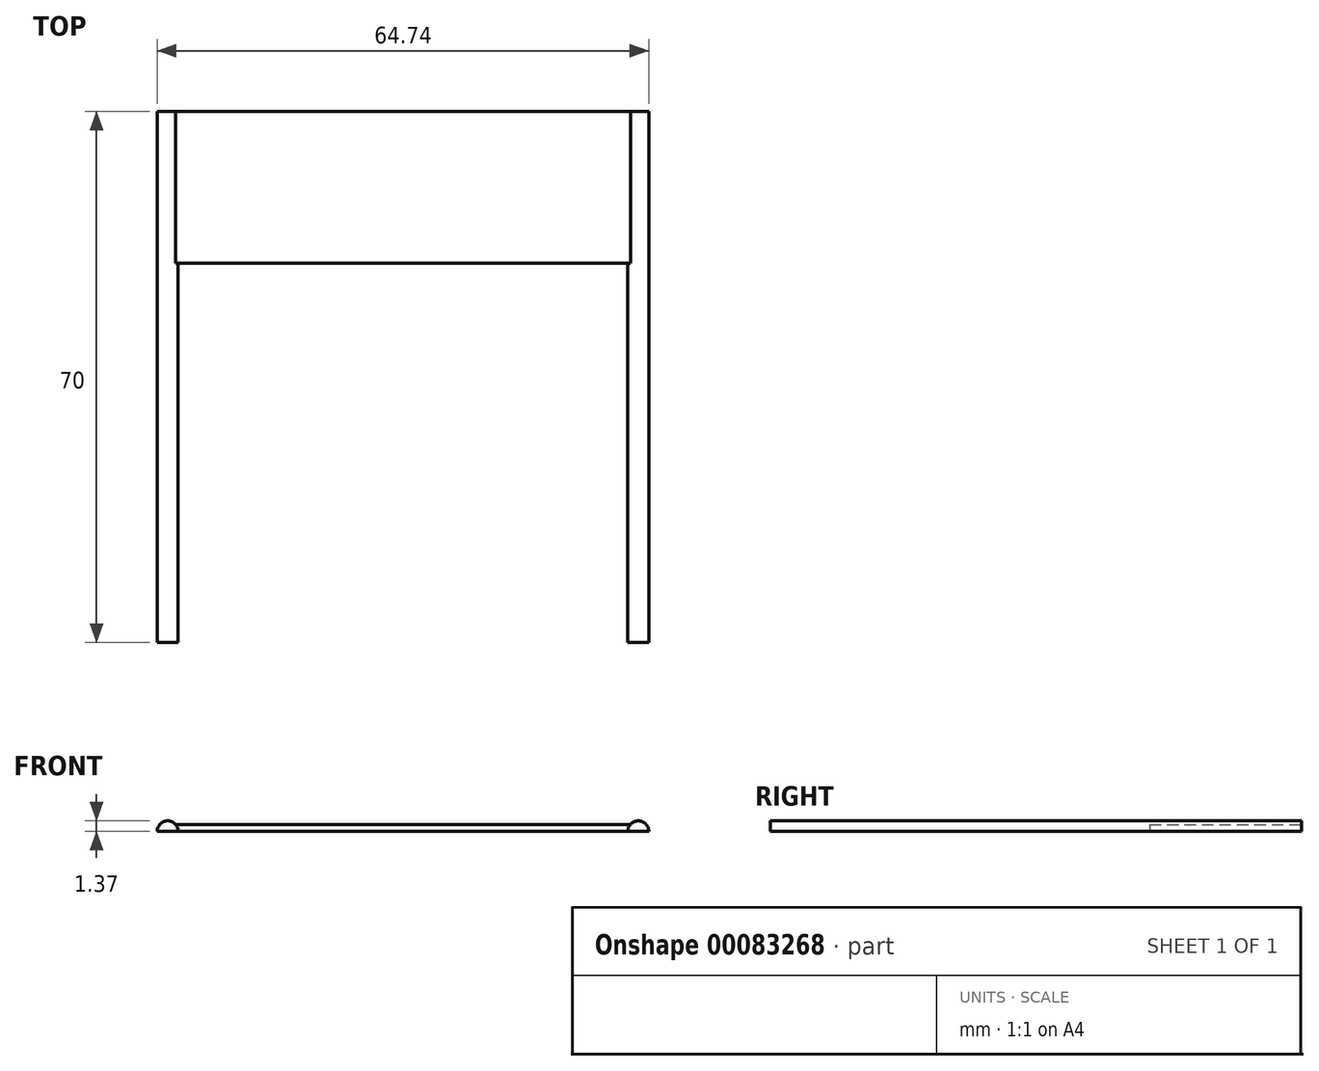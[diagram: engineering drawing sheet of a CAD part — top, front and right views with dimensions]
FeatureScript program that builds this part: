
annotation { "Feature Type Name" : "Feature", "Feature Type Description" : "" }
export const myFeature = defineFeature(function(context is Context, id is Id, definition is map)
    precondition{}
    {
        {
            var Q0;
            Q0=qCreatedBy(makeId("Top.planeOp"),FACE);
            var sketch = newSketch(context, id + "F0", { "sketchPlane" : qUnion([Q0])});
            skLineSegment(sketch, "E0.bottom", {"start": v(31, -10) * mm, "end": v(-31, -10) * mm});
            skLineSegment(sketch, "E0.top", {"start": v(31, 10) * mm, "end": v(-31, 10) * mm});
            skLineSegment(sketch, "E0.left", {"start": v(31, -10) * mm, "end": v(31, 10) * mm});
            skLineSegment(sketch, "E0.right", {"start": v(-31, -10) * mm, "end": v(-31, 10) * mm});
            skPoint(sketch, "E0.middle", {"position": v(0, 0) * mm});
            skSolve(sketch);
        }
        {
            var Q0;
            Q0=makeQuery(id+"F0.imprint","IMPRINT",FACE,{"disambiguationData":[TD([[makeQuery(id+"F0.imprint","IMPRINT",EDGE,{"derivedFrom":sQuery(id+"F0.wireOp",EDGE,"E0.bottom")}),-1.0]])]});
            extrude(context, id + "F1", {"entities" : qUnion([Q0]), "depth" : 0.9 * mm});
        }
        {
            var Q0;
            Q0=makeQuery(id+"F1.opExtrude","SWEPT_FACE",FACE,{"disambiguationData":[OSD([sQuery(id+"F0.wireOp",EDGE,"E0.bottom")])]});
            var sketch = newSketch(context, id + "F2", { "sketchPlane" : qUnion([Q0])});
            skArc(sketch, "E1", {"start": v(-32.37, 0) * mm, "mid": v(-31, 1.37) * mm, "end": v(-29.63, 0) * mm});
            skLineSegment(sketch, "E2", {"start": v(-32.37, 0) * mm, "end": v(-29.63, 0) * mm});
            skLineSegment(sketch, "E3.MirrorCS", {"start": v(32.37, 0) * mm, "end": v(29.63, 0) * mm});
            skArc(sketch, "E4.MirrorCS", {"start": v(32.37, 0) * mm, "mid": v(31, 1.37) * mm, "end": v(29.63, 0) * mm});
            skSolve(sketch);
        }
        {
            var Q0;
            {var subQ3=sQuery(id+"F0.wireOp",EDGE,"E0.bottom");var subQ6=makeQuery(id+"F1.opExtrude","SWEPT_EDGE",EDGE,{"disambiguationData":[OSD([subQ3,sQuery(id+"F0.wireOp",EDGE,"E0.right")])]});Q0=makeQuery(id+"F2.imprint","IMPRINT",FACE,{"disambiguationData":[TD([[makeQuery(id+"F2.imprint","IMPRINT",EDGE,{"derivedFrom":subQ6}),-1.0]])]});}
            var Q1;
            {var subQ2=sQuery(id+"F0.wireOp",EDGE,"E0.bottom");var subQ6=makeQuery(id+"F1.opExtrude","SWEPT_EDGE",EDGE,{"disambiguationData":[OSD([subQ2,sQuery(id+"F0.wireOp",EDGE,"E0.right")])]});Q1=makeQuery(id+"F2.imprint","IMPRINT",FACE,{"disambiguationData":[TD([[makeQuery(id+"F2.imprint","IMPRINT",EDGE,{"derivedFrom":subQ6}),1.0]])]});}
            var Q2;
            {var subQ1=sQuery(id+"F0.wireOp",EDGE,"E0.bottom");var subQ2=makeQuery(id+"F1.opExtrude","SWEPT_EDGE",EDGE,{"disambiguationData":[OSD([subQ1,sQuery(id+"F0.wireOp",EDGE,"E0.left")])]});Q2=makeQuery(id+"F2.imprint","IMPRINT",FACE,{"disambiguationData":[TD([[makeQuery(id+"F2.imprint","IMPRINT",EDGE,{"derivedFrom":subQ2}),-1.0]])]});}
            var Q3;
            {var subQ1=sQuery(id+"F0.wireOp",EDGE,"E0.bottom");var subQ2=makeQuery(id+"F1.opExtrude","SWEPT_EDGE",EDGE,{"disambiguationData":[OSD([subQ1,sQuery(id+"F0.wireOp",EDGE,"E0.left")])]});Q3=makeQuery(id+"F2.imprint","IMPRINT",FACE,{"disambiguationData":[TD([[makeQuery(id+"F2.imprint","IMPRINT",EDGE,{"derivedFrom":subQ2}),1.0]])]});}
            var Q4;
            Q4=makeQuery(id+"F1.opExtrude","SWEPT_FACE",FACE,{"disambiguationData":[OSD([sQuery(id+"F0.wireOp",EDGE,"E0.top")])]});
            extrude(context, id + "F3", {"entities" : qUnion([Q0, Q1, Q2, Q3]), "operationType" : NewBodyOperationType.ADD, "depth" : 50 * mm, "hasSecondDirection" : true, "secondDirectionBound" : SecondDirectionBoundingType.UP_TO_SURFACE, "secondDirectionOppositeDirection" : true, "secondDirectionBoundEntityFace" : qUnion([Q4]), "secondDirectionDepth" : 25 * mm});
        }
    });
